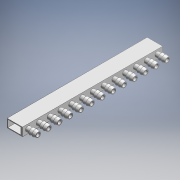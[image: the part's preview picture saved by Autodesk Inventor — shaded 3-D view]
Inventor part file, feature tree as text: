
AUTODESK INVENTOR PART (.ipt)
format: ipt  version: 2018 (Build 220112000, 112)  size: 243,200 bytes
history: native  units: in
note: dims shown in document units (in); Inventor stores cm internally (conversion verified against a paired STEP export)
features: other x7, extrude x4, sketch x2, pattern_linear x1, projected_geometry x1
ambient origin geometry x8: Origin, YZ Plane, XZ Plane, XY Plane, X Axis, Y Axis, Z Axis, Center Point
bodies: Body1 (feature_tree)
feature tree (15):
  other  "CrossSection1"
  other  "Silicone Fitting Plane"
  other  "Cap Plane"
  other  "Base Sketch"
  extrude  "Base"  Depth=0.0591in
  other  "Silicone Fitting"
  extrude  "Airflow Cut"  Depth=0.0591in
  pattern_linear  "Fitting Repetitions"  Spacing1=0.0197in  [1 undecoded]
  sketch  "Sketch22"  dims[d87=0.0197in d88=0.0787in d89=-1.0625in d90=0.7874in d1=0.0591in]
  extrude  "Extrusion21"  Depth=0.5906in
  extrude  "Extrusion24"  [1 undecoded]
  other  "Silicone Fitting Sketch"
  other  "Airflow Cut Sketch"
  projected_geometry  "Projected Loop7"
  sketch  "Sketch23"  dims[d2=0.0591in d3=0.0591in d4=0.0197in d5=0.5906in d6=-0.2067in d7=5.374in d8=0.0in d111=90.0deg d112=0.0787in d9=0.0in d10=5.1181in d11=0.4134in d12=-5.374in d141=0.0295in d142=0.0295in d143=0.2623in d144=0.502in d145=0.0591in d146=0.0295in d147=0.0295in d148=0.0295in d149=0.4134in d150=0.0in d155=0.0591in d156=0.0in]
note: 2 required parameter values undecoded (feature->parameter linkage not recoverable at this tier; creation-order binding heuristic only, values carry confidence <= 0.55)
